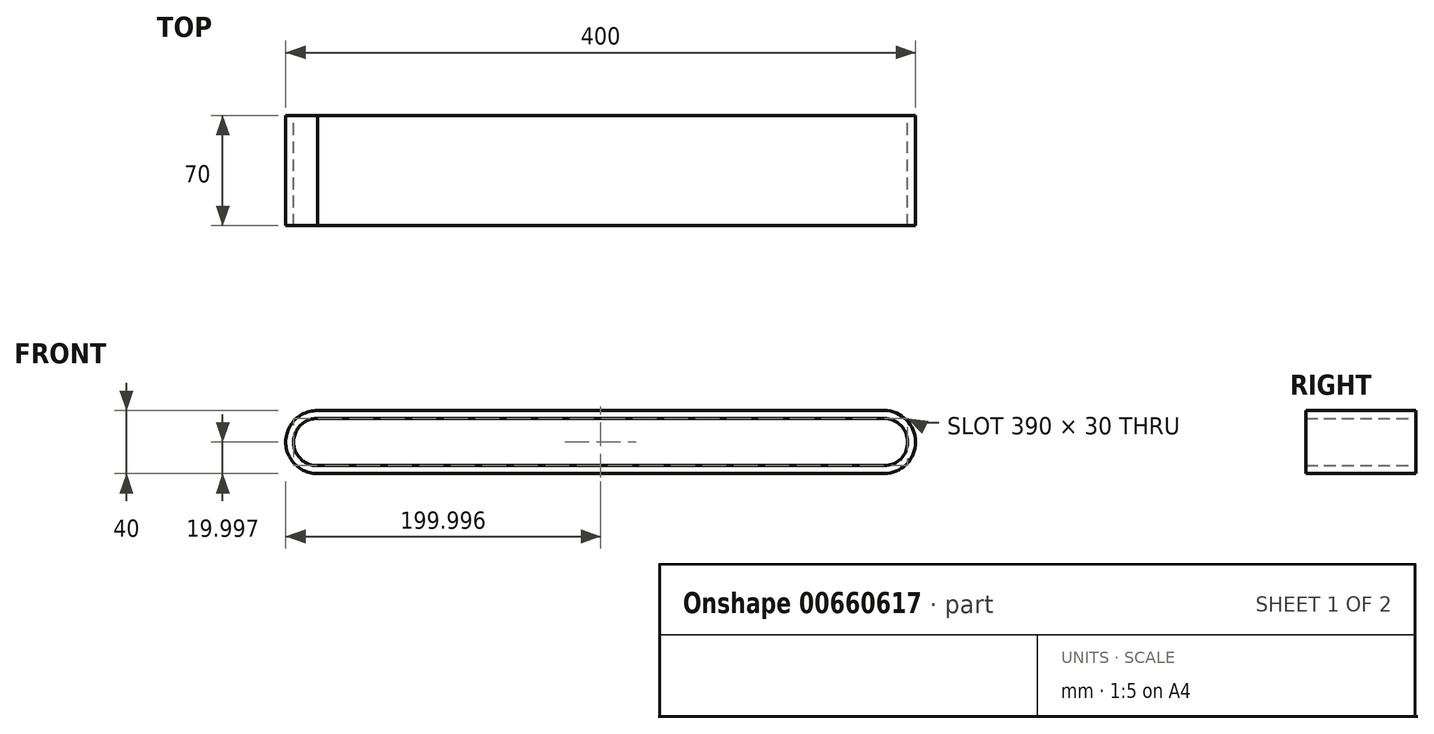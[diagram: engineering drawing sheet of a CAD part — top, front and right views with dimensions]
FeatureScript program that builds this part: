
annotation { "Feature Type Name" : "Feature", "Feature Type Description" : "" }
export const myFeature = defineFeature(function(context is Context, id is Id, definition is map)
    precondition{}
    {
        {
            var Q0;
            Q0=qCreatedBy(makeId("Front.planeOp"),FACE);
            var sketch = newSketch(context, id + "F0", { "sketchPlane" : qUnion([Q0])});
            skArc(sketch, "E0", {"start": v(-274.99, 20.85) * mm, "mid": v(-290.3, 6) * mm, "end": v(-275.3, -9.14) * mm});
            skArc(sketch, "E1", {"start": v(84.7, -9.14) * mm, "mid": v(99.7, 5.86) * mm, "end": v(84.7, 20.86) * mm});
            skArc(sketch, "E2.0", {"start": v(-274.99, 25.85) * mm, "mid": v(-295.3, 6) * mm, "end": v(-275.3, -14.14) * mm});
            skArc(sketch, "E3.0", {"start": v(84.7, -14.14) * mm, "mid": v(104.7, 5.86) * mm, "end": v(84.7, 25.86) * mm});
            skLineSegment(sketch, "E4", {"start": v(-274.99, 25.85) * mm, "end": v(84.7, 25.86) * mm});
            skLineSegment(sketch, "E5", {"start": v(84.7, -14.14) * mm, "end": v(-275.3, -14.14) * mm});
            skLineSegment(sketch, "E6", {"start": v(-274.99, 20.85) * mm, "end": v(84.7, 20.86) * mm});
            skLineSegment(sketch, "E7", {"start": v(84.7, -9.14) * mm, "end": v(-275.3, -9.14) * mm});
            skSolve(sketch);
        }
        {
            var Q0;
            Q0 = qSketchRegion(id + "F0", true);
            extrude(context, id + "F1", {"entities" : qUnion([Q0]), "depth" : 70 * mm, "offsetDistance" : 25 * mm});
        }
    });
